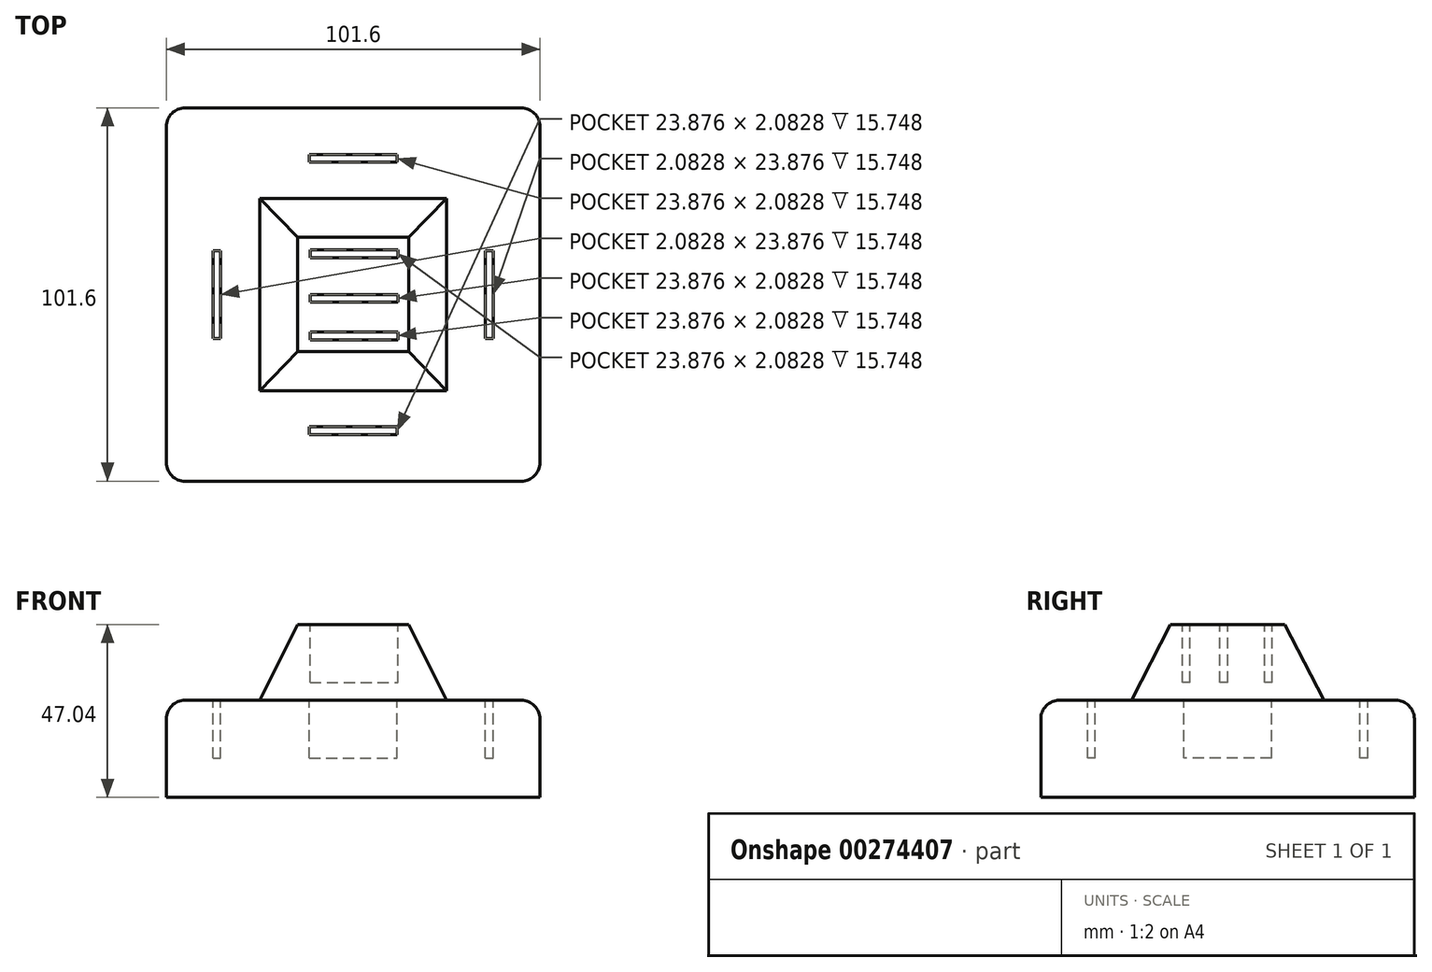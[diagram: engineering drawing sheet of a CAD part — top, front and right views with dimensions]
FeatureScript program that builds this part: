
annotation { "Feature Type Name" : "Feature", "Feature Type Description" : "" }
export const myFeature = defineFeature(function(context is Context, id is Id, definition is map)
    precondition{}
    {
        {
            var Q0;
            Q0=qCreatedBy(makeId("Top.planeOp"),FACE);
            var sketch = newSketch(context, id + "F0", { "sketchPlane" : qUnion([Q0])});
            skLineSegment(sketch, "E0", {"start": v(-47.67, 75.12) * mm, "end": v(-47.67, -26.48) * mm});
            skLineSegment(sketch, "E1", {"start": v(-47.67, -26.48) * mm, "end": v(53.93, -26.48) * mm});
            skLineSegment(sketch, "E2", {"start": v(53.93, -26.48) * mm, "end": v(53.93, 75.12) * mm});
            skLineSegment(sketch, "E3", {"start": v(53.93, 75.12) * mm, "end": v(-47.67, 75.12) * mm});
            skSolve(sketch);
        }
        {
            var Q0;
            Q0 = qSketchRegion(id + "F0", true);
            extrude(context, id + "F1", {"entities" : qUnion([Q0]), "depth" : 50.8 * mm});
        }
        {
            var Q0;
            Q0=makeQuery(id+"F1.opExtrude","CAP_FACE",FACE,{"disambiguationData":[OSD([sQuery(id+"F0.wireOp",EDGE,"E0"),sQuery(id+"F0.wireOp",EDGE,"E1"),sQuery(id+"F0.wireOp",EDGE,"E2"),sQuery(id+"F0.wireOp",EDGE,"E3")])],"isStart":false});
            var sketch = newSketch(context, id + "F2", { "sketchPlane" : qUnion([Q0])});
            skLineSegment(sketch, "E4.bottom", {"start": v(-22.3, -1.84) * mm, "end": v(28.58, -1.84) * mm});
            skLineSegment(sketch, "E4.top", {"start": v(-22.3, 50.48) * mm, "end": v(28.58, 50.48) * mm});
            skLineSegment(sketch, "E4.left", {"start": v(-22.3, -1.84) * mm, "end": v(-22.3, 50.48) * mm});
            skLineSegment(sketch, "E4.right", {"start": v(28.58, -1.84) * mm, "end": v(28.58, 50.48) * mm});
            skPoint(sketch, "E4.middle", {"position": v(3.13, 24.32) * mm});
            skSolve(sketch);
        }
        {
            var Q0;
            {var subQ3=sQuery(id+"F2.wireOp",EDGE,"E4.bottom");var subQ5=sQuery(id+"F2.wireOp",EDGE,"E4.right");var subQ6=makeQuery(id+"F2.imprint","INTERSECT",VERTEX,{"derivedFrom":[subQ3,subQ5]});Q0=makeQuery(id+"F2.imprint","IMPRINT",FACE,{"disambiguationData":[TD([[makeQuery(id+"F2.imprint","IMPRINT",EDGE,{"disambiguationData":[TD([[subQ6,1.0]])],"derivedFrom":subQ3}),1.0]])]});}
            cPlane(context, id + "F3", {"entities" : qUnion([Q0]), "cplaneType" : CPlaneType.OFFSET, "offset" : 50.8 * mm, "width" : 152.4 * mm, "height" : 152.4 * mm});
        }
        {
            var Q0;
            Q0=qCreatedBy(id+"F3.planeOp",FACE);
            var sketch = newSketch(context, id + "F4", { "sketchPlane" : qUnion([Q0])});
            skPoint(sketch, "E5.0", {"position": v(3.13, 24.32) * mm});
            skSolve(sketch);
        }
        {
            var Q1;
            Q1=sQuery(id+"F4.wireOp",VERTEX,"E5.0");
            var Q2;
            Q2=makeQuery(id+"F2.imprint","IMPRINT",FACE,{"disambiguationData":[TD([[makeQuery(id+"F2.imprint","IMPRINT",EDGE,{"derivedFrom":sQuery(id+"F2.wireOp",EDGE,"E4.bottom")}),1.0]])]});
            loft(context, id + "F5", {"operationType" : NewBodyOperationType.ADD, "sheetProfilesArray" : [{ "sheetProfileEntities" : qUnion([Q1]) }, { "sheetProfileEntities" : qUnion([Q2]) }]});
        }
        {
            var Q0;
            Q0=makeQuery(id+"F1.opExtrude","CAP_EDGE",EDGE,{"disambiguationData":[OSD([sQuery(id+"F0.wireOp",EDGE,"E1")])],"isStart":false});
            var Q1;
            Q1=makeQuery(id+"F1.opExtrude","CAP_EDGE",EDGE,{"disambiguationData":[OSD([sQuery(id+"F0.wireOp",EDGE,"E0")])],"isStart":false});
            var Q2;
            Q2=makeQuery(id+"F1.opExtrude","CAP_EDGE",EDGE,{"disambiguationData":[OSD([sQuery(id+"F0.wireOp",EDGE,"E3")])],"isStart":false});
            var Q3;
            Q3=makeQuery(id+"F1.opExtrude","CAP_EDGE",EDGE,{"disambiguationData":[OSD([sQuery(id+"F0.wireOp",EDGE,"E2")])],"isStart":false});
            fillet(context, id + "F6", {"entities" : qUnion([Q0, Q1, Q2, Q3]), "radius" : 5.08 * mm, "tangentPropagation" : true, "allowEdgeOverflow" : false});
        }
        {
            var Q0;
            Q0=makeQuery(id+"F6.opFillet","BLEND_EDGE",EDGE,{"blendedFrom":[makeQuery(id+"F1.opExtrude","CAP_EDGE",EDGE,{"disambiguationData":[OSD([sQuery(id+"F0.wireOp",EDGE,"E2")])],"isStart":false}),makeQuery(id+"F1.opExtrude","CAP_EDGE",EDGE,{"disambiguationData":[OSD([sQuery(id+"F0.wireOp",EDGE,"E3")])],"isStart":false})],"blendedInto":[]});
            var Q1;
            Q1=makeQuery(id+"F6.opFillet","BLEND_EDGE",EDGE,{"blendedFrom":[makeQuery(id+"F1.opExtrude","CAP_EDGE",EDGE,{"disambiguationData":[OSD([sQuery(id+"F0.wireOp",EDGE,"E1")])],"isStart":false}),makeQuery(id+"F1.opExtrude","CAP_EDGE",EDGE,{"disambiguationData":[OSD([sQuery(id+"F0.wireOp",EDGE,"E2")])],"isStart":false})],"blendedInto":[]});
            var Q2;
            Q2=makeQuery(id+"F6.opFillet","BLEND_EDGE",EDGE,{"blendedFrom":[makeQuery(id+"F1.opExtrude","CAP_EDGE",EDGE,{"disambiguationData":[OSD([sQuery(id+"F0.wireOp",EDGE,"E0")])],"isStart":false}),makeQuery(id+"F1.opExtrude","CAP_EDGE",EDGE,{"disambiguationData":[OSD([sQuery(id+"F0.wireOp",EDGE,"E1")])],"isStart":false})],"blendedInto":[]});
            var Q3;
            Q3=makeQuery(id+"F6.opFillet","BLEND_EDGE",EDGE,{"blendedFrom":[makeQuery(id+"F1.opExtrude","CAP_EDGE",EDGE,{"disambiguationData":[OSD([sQuery(id+"F0.wireOp",EDGE,"E0")])],"isStart":false}),makeQuery(id+"F1.opExtrude","CAP_EDGE",EDGE,{"disambiguationData":[OSD([sQuery(id+"F0.wireOp",EDGE,"E3")])],"isStart":false})],"blendedInto":[]});
            fillet(context, id + "F7", {"entities" : qUnion([Q0, Q1, Q2, Q3]), "radius" : 5.08 * mm, "tangentPropagation" : true, "allowEdgeOverflow" : false});
        }
        {
            var Q0;
            Q0=qCreatedBy(makeId("Front.planeOp"),FACE);
            var sketch = newSketch(context, id + "F8", { "sketchPlane" : qUnion([Q0])});
            skLineSegment(sketch, "E6.bottom", {"start": v(-16.13, 71.42) * mm, "end": v(20.86, 71.42) * mm});
            skLineSegment(sketch, "E6.top", {"start": v(-16.13, 104.1) * mm, "end": v(20.86, 104.1) * mm});
            skLineSegment(sketch, "E6.left", {"start": v(-16.13, 71.42) * mm, "end": v(-16.13, 104.1) * mm});
            skLineSegment(sketch, "E6.right", {"start": v(20.86, 71.42) * mm, "end": v(20.86, 104.1) * mm});
            skSolve(sketch);
        }
        {
            var Q0;
            Q0 = qSketchRegion(id + "F8", true);
            extrude(context, id + "F9", {"entities" : qUnion([Q0]), "operationType" : NewBodyOperationType.REMOVE, "oppositeDirection" : true, "depth" : 43.43 * mm});
        }
        {
            var Q0;
            Q0=makeQuery(id+"F2.imprint","IMPRINT",FACE,{"disambiguationData":[TD([[makeQuery(id+"F2.imprint","IMPRINT",EDGE,{"derivedFrom":sQuery(id+"F2.wireOp",EDGE,"E4.bottom")}),-1.0]])]});
            var sketch = newSketch(context, id + "F10", { "sketchPlane" : qUnion([Q0])});
            skLineSegment(sketch, "E7.bottom", {"start": v(-34.97, 36.25) * mm, "end": v(-32.88, 36.25) * mm});
            skLineSegment(sketch, "E7.top", {"start": v(-34.97, 12.38) * mm, "end": v(-32.88, 12.38) * mm});
            skLineSegment(sketch, "E7.left", {"start": v(-34.97, 36.25) * mm, "end": v(-34.97, 12.38) * mm});
            skLineSegment(sketch, "E7.right", {"start": v(-32.88, 36.25) * mm, "end": v(-32.88, 12.38) * mm});
            skLineSegment(sketch, "E8.bottom", {"start": v(-8.8, 62.42) * mm, "end": v(15.07, 62.42) * mm});
            skLineSegment(sketch, "E8.top", {"start": v(-8.8, 60.33) * mm, "end": v(15.07, 60.33) * mm});
            skLineSegment(sketch, "E8.left", {"start": v(-8.8, 62.42) * mm, "end": v(-8.8, 60.33) * mm});
            skLineSegment(sketch, "E8.right", {"start": v(15.07, 62.42) * mm, "end": v(15.07, 60.33) * mm});
            skLineSegment(sketch, "E9.bottom", {"start": v(39.15, 36.25) * mm, "end": v(41.23, 36.25) * mm});
            skLineSegment(sketch, "E9.top", {"start": v(39.15, 12.38) * mm, "end": v(41.23, 12.38) * mm});
            skLineSegment(sketch, "E9.left", {"start": v(39.15, 36.25) * mm, "end": v(39.15, 12.38) * mm});
            skLineSegment(sketch, "E9.right", {"start": v(41.23, 36.25) * mm, "end": v(41.23, 12.38) * mm});
            skLineSegment(sketch, "E10.bottom", {"start": v(-8.8, -11.7) * mm, "end": v(15.07, -11.7) * mm});
            skLineSegment(sketch, "E10.top", {"start": v(-8.8, -13.78) * mm, "end": v(15.07, -13.78) * mm});
            skLineSegment(sketch, "E10.left", {"start": v(-8.8, -11.7) * mm, "end": v(-8.8, -13.78) * mm});
            skLineSegment(sketch, "E10.right", {"start": v(15.07, -11.7) * mm, "end": v(15.07, -13.78) * mm});
            skSolve(sketch);
        }
        {
            var Q0;
            Q0 = qSketchRegion(id + "F10", true);
            extrude(context, id + "F11", {"entities" : qUnion([Q0]), "operationType" : NewBodyOperationType.REMOVE, "oppositeDirection" : true, "depth" : 15.75 * mm});
        }
        {
            var Q0;
            Q0=makeQuery(id+"F9.boolean.opBoolean","COPY",FACE,{"derivedFrom":makeQuery(id+"F9.opExtrude","SWEPT_FACE",FACE,{"disambiguationData":[OSD([sQuery(id+"F8.wireOp",EDGE,"E6.bottom")])]})});
            var sketch = newSketch(context, id + "F12", { "sketchPlane" : qUnion([Q0])});
            skLineSegment(sketch, "E11", {"start": v(-11.98, 24.32) * mm, "end": v(18.25, 24.32) * mm});
            skLineSegment(sketch, "E12", {"start": v(3.13, 8.77) * mm, "end": v(3.13, 39.86) * mm});
            skLineSegment(sketch, "E13.bottom", {"start": v(-8.6, 36.45) * mm, "end": v(15.28, 36.45) * mm});
            skLineSegment(sketch, "E13.top", {"start": v(-8.6, 34.37) * mm, "end": v(15.28, 34.37) * mm});
            skLineSegment(sketch, "E13.left", {"start": v(-8.6, 36.45) * mm, "end": v(-8.6, 34.37) * mm});
            skLineSegment(sketch, "E13.right", {"start": v(15.28, 36.45) * mm, "end": v(15.28, 34.37) * mm});
            skPoint(sketch, "E14.firstSnap0", {"position": v(-8.6, 35.41) * mm});
            skLineSegment(sketch, "E14.bottom", {"start": v(-8.6, 24.32) * mm, "end": v(15.28, 24.32) * mm});
            skLineSegment(sketch, "E14.top", {"start": v(-8.6, 22.23) * mm, "end": v(15.28, 22.23) * mm});
            skLineSegment(sketch, "E14.left", {"start": v(-8.6, 24.32) * mm, "end": v(-8.6, 22.23) * mm});
            skLineSegment(sketch, "E14.right", {"start": v(15.28, 24.32) * mm, "end": v(15.28, 22.23) * mm});
            skLineSegment(sketch, "E15.bottom", {"start": v(-8.6, 14.11) * mm, "end": v(15.28, 14.11) * mm});
            skLineSegment(sketch, "E15.top", {"start": v(-8.6, 12.03) * mm, "end": v(15.28, 12.03) * mm});
            skLineSegment(sketch, "E15.left", {"start": v(-8.6, 14.11) * mm, "end": v(-8.6, 12.03) * mm});
            skLineSegment(sketch, "E15.right", {"start": v(15.28, 14.11) * mm, "end": v(15.28, 12.03) * mm});
            skSolve(sketch);
        }
        {
            var Q0;
            Q0 = qSketchRegion(id + "F12", true);
            extrude(context, id + "F13", {"entities" : qUnion([Q0]), "operationType" : NewBodyOperationType.REMOVE, "oppositeDirection" : true, "depth" : 15.75 * mm});
        }
        {
            var Q0;
            Q0=makeQuery(id+"F0.imprint","IMPRINT",FACE,{"disambiguationData":[TD([[makeQuery(id+"F0.imprint","IMPRINT",EDGE,{"derivedFrom":sQuery(id+"F0.wireOp",EDGE,"E0")}),1.0]])]});
            extrude(context, id + "F14", {"entities" : qUnion([Q0]), "operationType" : NewBodyOperationType.REMOVE, "depth" : 24.38 * mm});
        }
    });
